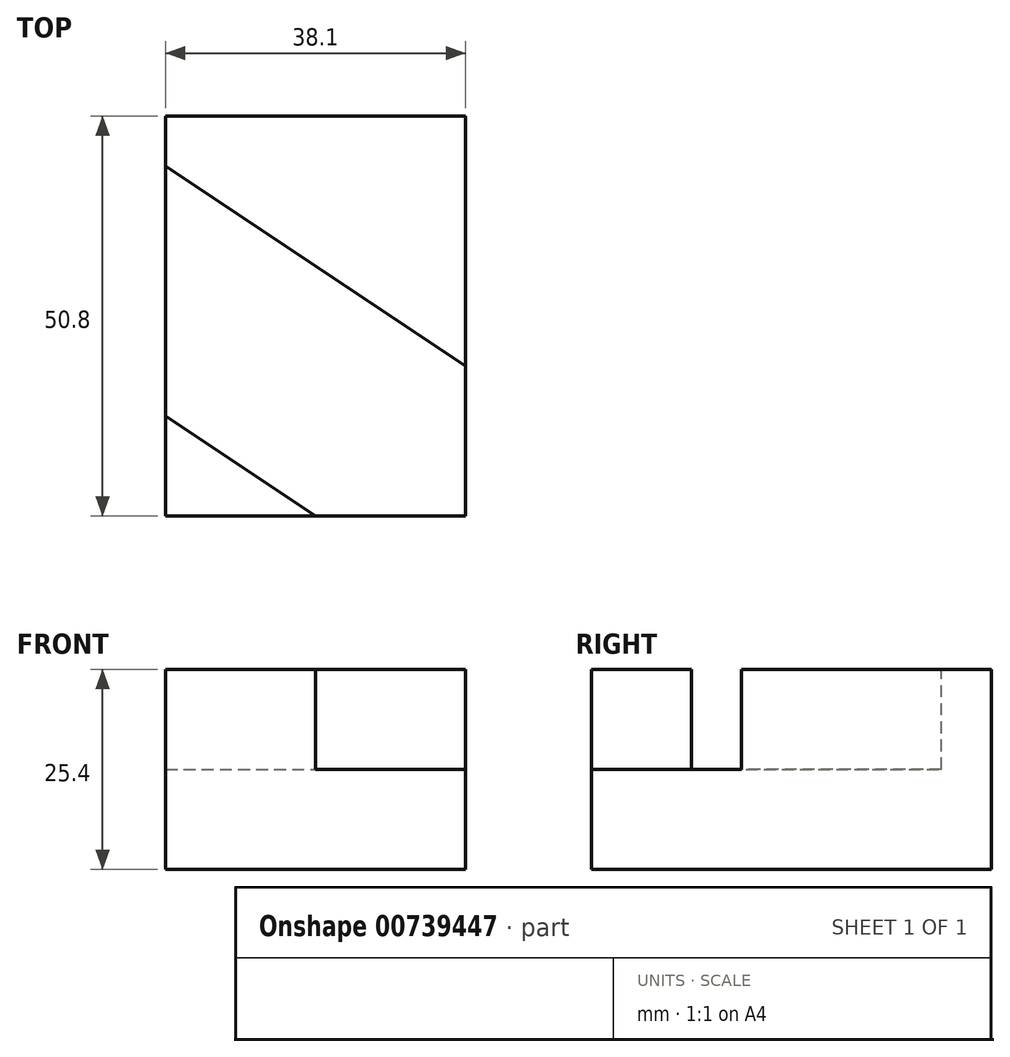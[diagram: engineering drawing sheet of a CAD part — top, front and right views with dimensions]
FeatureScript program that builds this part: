
annotation { "Feature Type Name" : "Feature", "Feature Type Description" : "" }
export const myFeature = defineFeature(function(context is Context, id is Id, definition is map)
    precondition{}
    {
        {
            var Q0;
            Q0=qCreatedBy(makeId("Top.planeOp"),FACE);
            var sketch = newSketch(context, id + "F0", { "sketchPlane" : qUnion([Q0])});
            skLineSegment(sketch, "E0.bottom", {"start": v(0, 0) * mm, "end": v(38.1, 0) * mm});
            skLineSegment(sketch, "E0.top", {"start": v(0, 50.8) * mm, "end": v(38.1, 50.8) * mm});
            skLineSegment(sketch, "E0.left", {"start": v(0, 0) * mm, "end": v(0, 50.8) * mm});
            skLineSegment(sketch, "E0.right", {"start": v(38.1, 0) * mm, "end": v(38.1, 50.8) * mm});
            skSolve(sketch);
        }
        {
            var Q0;
            Q0=makeQuery(id+"F0.imprint","IMPRINT",FACE,{"disambiguationData":[TD([[makeQuery(id+"F0.imprint","IMPRINT",EDGE,{"derivedFrom":sQuery(id+"F0.wireOp",EDGE,"E0.bottom")}),1.0]])]});
            extrude(context, id + "F1", {"entities" : qUnion([Q0]), "depth" : 25.4 * mm, "offsetDistance" : 25.4 * mm});
        }
        {
            var Q0;
            Q0=makeQuery(id+"F1.opExtrude","CAP_FACE",FACE,{"disambiguationData":[OSD([sQuery(id+"F0.wireOp",EDGE,"E0.bottom"),sQuery(id+"F0.wireOp",EDGE,"E0.top"),sQuery(id+"F0.wireOp",EDGE,"E0.left"),sQuery(id+"F0.wireOp",EDGE,"E0.right")])],"isStart":false});
            var sketch = newSketch(context, id + "F2", { "sketchPlane" : qUnion([Q0])});
            skLineSegment(sketch, "E1", {"start": v(0, 44.45) * mm, "end": v(38.1, 19.05) * mm});
            skLineSegment(sketch, "E2", {"start": v(38.1, 19.05) * mm, "end": v(38.1, 0) * mm});
            skLineSegment(sketch, "E3", {"start": v(38.1, 0) * mm, "end": v(19.05, 0) * mm});
            skLineSegment(sketch, "E4", {"start": v(19.05, 0) * mm, "end": v(0, 12.7) * mm});
            skLineSegment(sketch, "E5", {"start": v(0, 12.7) * mm, "end": v(0, 44.45) * mm});
            skSolve(sketch);
        }
        {
            var Q0;
            Q0=makeQuery(id+"F2.imprint","IMPRINT",FACE,{"disambiguationData":[TD([[makeQuery(id+"F2.imprint","IMPRINT",EDGE,{"derivedFrom":sQuery(id+"F2.wireOp",EDGE,"E1")}),-1.0]])]});
            extrude(context, id + "F3", {"entities" : qUnion([Q0]), "operationType" : NewBodyOperationType.REMOVE, "oppositeDirection" : true, "depth" : 12.7 * mm, "offsetDistance" : 25.4 * mm});
        }
    });
